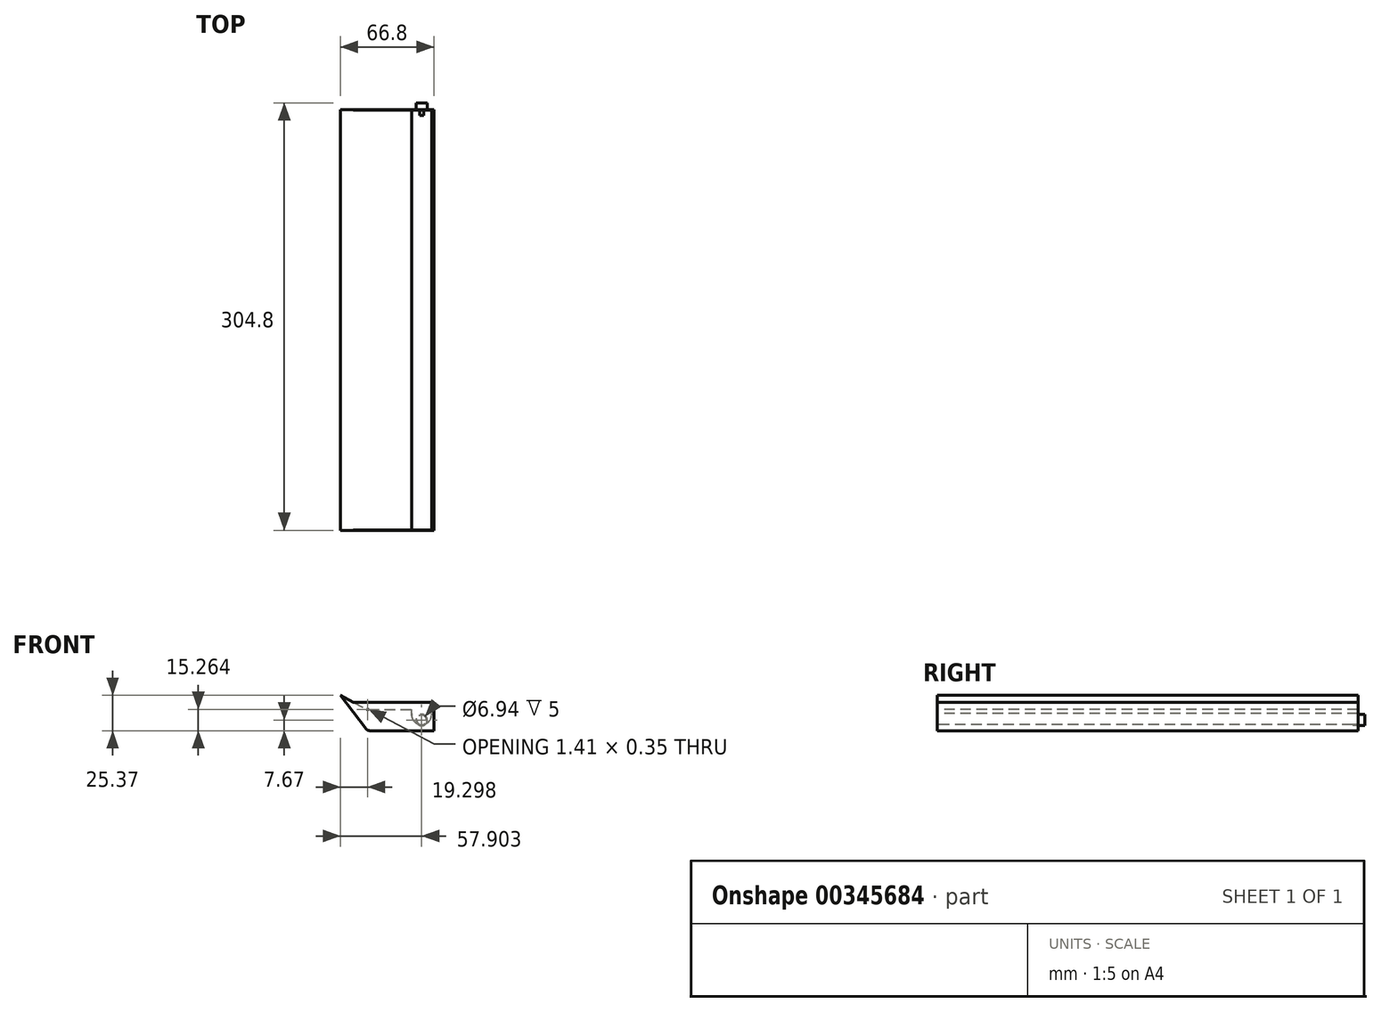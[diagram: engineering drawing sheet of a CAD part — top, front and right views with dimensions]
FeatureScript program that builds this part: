
annotation { "Feature Type Name" : "Feature", "Feature Type Description" : "" }
export const myFeature = defineFeature(function(context is Context, id is Id, definition is map)
    precondition{}
    {
        {
            var Q0;
            Q0=qCreatedBy(makeId("Front.planeOp"),FACE);
            var sketch = newSketch(context, id + "F0", { "sketchPlane" : qUnion([Q0])});
            skLineSegment(sketch, "E0", {"start": v(-53.15, 39.65) * mm, "end": v(-34.56, 29.72) * mm});
            skLineSegment(sketch, "E1", {"start": v(-33.15, 29.37) * mm, "end": v(-2.4, 29.37) * mm});
            skLineSegment(sketch, "E2", {"start": v(-2.4, 29.37) * mm, "end": v(-2.4, 26.46) * mm});
            skLineSegment(sketch, "E3", {"start": v(-2.4, 14.37) * mm, "end": v(-32.4, 14.37) * mm});
            skLineSegment(sketch, "E4", {"start": v(-34.8, 15.55) * mm, "end": v(-53.15, 39.65) * mm});
            skPoint(sketch, "E5.visualSharp", {"position": v(-33.9, 29.37) * mm});
            skArc(sketch, "E5.filletArc", {"start": v(-34.56, 29.72) * mm, "mid": v(-33.87, 29.46) * mm, "end": v(-33.15, 29.37) * mm});
            skPoint(sketch, "E6.visualSharp", {"position": v(-33.9, 14.37) * mm});
            skArc(sketch, "E6.filletArc", {"start": v(-34.8, 15.55) * mm, "mid": v(-33.74, 14.68) * mm, "end": v(-32.4, 14.37) * mm});
            skLineSegment(sketch, "E7", {"start": v(13.65, 14.28) * mm, "end": v(-2.4, 14.37) * mm});
            skLineSegment(sketch, "E8", {"start": v(13.65, 26.46) * mm, "end": v(13.65, 14.28) * mm});
            skLineSegment(sketch, "E9", {"start": v(13.65, 26.46) * mm, "end": v(13.65, 29.37) * mm});
            skLineSegment(sketch, "E10", {"start": v(13.65, 29.37) * mm, "end": v(11.79, 29.37) * mm});
            skLineSegment(sketch, "E11", {"start": v(11.79, 29.37) * mm, "end": v(11.79, 26.46) * mm});
            skArc(sketch, "E12", {"start": v(-2.4, 26.46) * mm, "mid": v(4.7, 18.65) * mm, "end": v(11.79, 26.46) * mm});
            skSolve(sketch);
        }
        {
            var Q0;
            Q0=qSketchRegion(id+"F0",true);
            extrude(context, id + "F1", {"entities" : qUnion([Q0]), "oppositeDirection" : true, "depth" : 300 * mm});
        }
        {
            var Q0;
            Q0=makeQuery(id+"F1.opExtrude","CAP_FACE",FACE,{"disambiguationData":[OSD([sQuery(id+"F0.wireOp",EDGE,"E0"),sQuery(id+"F0.wireOp",EDGE,"E1"),sQuery(id+"F0.wireOp",EDGE,"E2"),sQuery(id+"F0.wireOp",EDGE,"E3"),sQuery(id+"F0.wireOp",EDGE,"E4"),sQuery(id+"F0.wireOp",EDGE,"E5.filletArc"),sQuery(id+"F0.wireOp",EDGE,"E6.filletArc"),sQuery(id+"F0.wireOp",EDGE,"E7"),sQuery(id+"F0.wireOp",EDGE,"E8"),sQuery(id+"F0.wireOp",EDGE,"E9"),sQuery(id+"F0.wireOp",EDGE,"E10"),sQuery(id+"F0.wireOp",EDGE,"E11"),sQuery(id+"F0.wireOp",EDGE,"E12")])],"isStart":true});
            var sketch = newSketch(context, id + "F2", { "sketchPlane" : qUnion([Q0])});
            skLineSegment(sketch, "E13", {"start": v(-43.85, 34.68) * mm, "end": v(13.65, 34.68) * mm});
            skLineSegment(sketch, "E14", {"start": v(13.65, 34.68) * mm, "end": v(13.65, 29.37) * mm});
            skLineSegment(sketch, "E15", {"start": v(-43.85, 34.68) * mm, "end": v(-34.56, 29.72) * mm});
            skLineSegment(sketch, "E16", {"start": v(-34.56, 29.72) * mm, "end": v(-33.15, 29.37) * mm});
            skLineSegment(sketch, "E17", {"start": v(-33.15, 29.37) * mm, "end": v(-2.4, 29.37) * mm});
            skLineSegment(sketch, "E18", {"start": v(-2.4, 29.37) * mm, "end": v(-2.5, 18.65) * mm});
            skPoint(sketch, "E18.endSnap0", {"position": v(4.7, 18.65) * mm});
            skLineSegment(sketch, "E19", {"start": v(-2.5, 18.65) * mm, "end": v(13.65, 18.65) * mm});
            skLineSegment(sketch, "E20", {"start": v(13.65, 18.65) * mm, "end": v(13.65, 29.37) * mm});
            skSolve(sketch);
        }
        {
            var Q0;
            Q0=qSketchRegion(id+"F2",true);
            extrude(context, id + "F3", {"entities" : qUnion([Q0]), "operationType" : NewBodyOperationType.ADD, "oppositeDirection" : true, "depth" : .2 * mm});
        }
        {
            var Q0;
            Q0=makeQuery(id+"F1.opExtrude","CAP_FACE",FACE,{"disambiguationData":[OSD([sQuery(id+"F0.wireOp",EDGE,"E0"),sQuery(id+"F0.wireOp",EDGE,"E1"),sQuery(id+"F0.wireOp",EDGE,"E2"),sQuery(id+"F0.wireOp",EDGE,"E3"),sQuery(id+"F0.wireOp",EDGE,"E4"),sQuery(id+"F0.wireOp",EDGE,"E5.filletArc"),sQuery(id+"F0.wireOp",EDGE,"E6.filletArc"),sQuery(id+"F0.wireOp",EDGE,"E7"),sQuery(id+"F0.wireOp",EDGE,"E8"),sQuery(id+"F0.wireOp",EDGE,"E9"),sQuery(id+"F0.wireOp",EDGE,"E10"),sQuery(id+"F0.wireOp",EDGE,"E11"),sQuery(id+"F0.wireOp",EDGE,"E12")])],"isStart":false});
            var sketch = newSketch(context, id + "F4", { "sketchPlane" : qUnion([Q0])});
            skLineSegment(sketch, "E21", {"start": v(43.85, 34.68) * mm, "end": v(-13.65, 34.68) * mm});
            skLineSegment(sketch, "E22", {"start": v(-13.65, 34.68) * mm, "end": v(-13.65, 18.65) * mm});
            skPoint(sketch, "E22.endSnap0", {"position": v(-4.7, 18.65) * mm});
            skLineSegment(sketch, "E23", {"start": v(-13.65, 18.65) * mm, "end": v(2.4, 18.65) * mm});
            skLineSegment(sketch, "E24", {"start": v(2.4, 18.65) * mm, "end": v(2.4, 29.37) * mm});
            skLineSegment(sketch, "E25", {"start": v(2.4, 29.37) * mm, "end": v(33.15, 29.37) * mm});
            skLineSegment(sketch, "E26", {"start": v(33.15, 29.37) * mm, "end": v(34.56, 29.72) * mm});
            skLineSegment(sketch, "E27", {"start": v(34.56, 29.72) * mm, "end": v(43.85, 34.68) * mm});
            skSolve(sketch);
        }
        {
            var Q0;
            Q0=qSketchRegion(id+"F4",true);
            extrude(context, id + "F5", {"entities" : qUnion([Q0]), "operationType" : NewBodyOperationType.ADD, "oppositeDirection" : true, "depth" : .2 * mm});
        }
        {
            var Q0;
            Q0=makeQuery(id+"F5.boolean.opBoolean","MERGE",FACE,{"derivedFrom":[makeQuery(id+"F3.boolean.opBoolean","MERGE",FACE,{"derivedFrom":[makeQuery(id+"F1.opExtrude","SWEPT_FACE",FACE,{"disambiguationData":[OSD([sQuery(id+"F0.wireOp",EDGE,"E8"),sQuery(id+"F0.wireOp",EDGE,"E9")])]}),makeQuery(id+"F3.opExtrude","SWEPT_FACE",FACE,{"disambiguationData":[OSD([sQuery(id+"F2.wireOp",EDGE,"E14"),sQuery(id+"F2.wireOp",EDGE,"E20")])]})]}),makeQuery(id+"F5.opExtrude","SWEPT_FACE",FACE,{"disambiguationData":[OSD([sQuery(id+"F4.wireOp",EDGE,"E22")])]})]});
            var sketch = newSketch(context, id + "F6", { "sketchPlane" : qUnion([Q0])});
            skLineSegment(sketch, "E28", {"start": v(0.2, 34.68) * mm, "end": v(300, 34.68) * mm});
            skLineSegment(sketch, "E29", {"start": v(300, 34.68) * mm, "end": v(299.8, 29.37) * mm});
            skLineSegment(sketch, "E30", {"start": v(299.8, 29.37) * mm, "end": v(0.2, 29.37) * mm});
            skLineSegment(sketch, "E31", {"start": v(0.2, 29.37) * mm, "end": v(0.2, 34.68) * mm});
            skSolve(sketch);
        }
        {
            var Q0;
            Q0=qSketchRegion(id+"F6",true);
            extrude(context, id + "F7", {"entities" : qUnion([Q0]), "oppositeDirection" : true, "depth" : 1.8 * mm});
        }
        {
            var Q0;
            Q0=makeQuery(id+"F5.opExtrude","CAP_FACE",FACE,{"disambiguationData":[OSD([sQuery(id+"F4.wireOp",EDGE,"E21"),sQuery(id+"F4.wireOp",EDGE,"E22"),sQuery(id+"F4.wireOp",EDGE,"E23"),sQuery(id+"F4.wireOp",EDGE,"E24"),sQuery(id+"F4.wireOp",EDGE,"E25"),sQuery(id+"F4.wireOp",EDGE,"E26"),sQuery(id+"F4.wireOp",EDGE,"E27")])],"isStart":false});
            var sketch = newSketch(context, id + "F8", { "sketchPlane" : qUnion([Q0])});
            skCircle(sketch, "E32", {"center": v(4.75, 21.95) * mm, "radius": 3.47 * mm});
            skCircle(sketch, "E33", {"center": v(4.75, 21.95) * mm, "radius": 4.03 * mm});
            skCircle(sketch, "E34", {"center": v(4.75, 21.95) * mm, "radius": 3.4 * mm});
            skSolve(sketch);
        }
        {
            var Q0;
            Q0=qSketchRegion(id+"F8",true);
            extrude(context, id + "F9", {"entities" : qUnion([Q0]), "operationType" : NewBodyOperationType.REMOVE, "depth" : 0.01 * mm});
        }
        {
            var Q0;
            Q0=qSketchRegion(id+"F8",true);
            extrude(context, id + "F10", {"entities" : qUnion([Q0]), "operationType" : NewBodyOperationType.ADD, "oppositeDirection" : true, "depth" : 5 * mm});
        }
        {
            var Q0;
            Q0=makeQuery(id+"F10.boolean.opBoolean","SPLIT",FACE,{"disambiguationData":[TD([makeQuery(id+"F10.opExtrude","SWEPT_FACE",FACE,{"disambiguationData":[OSD([sQuery(id+"F8.wireOp",EDGE,"E32")])]})])],"derivedFrom":makeQuery(id+"F5.boolean.opBoolean","MERGE",FACE,{"derivedFrom":[makeQuery(id+"F1.opExtrude","CAP_FACE",FACE,{"disambiguationData":[OSD([sQuery(id+"F0.wireOp",EDGE,"E0"),sQuery(id+"F0.wireOp",EDGE,"E1"),sQuery(id+"F0.wireOp",EDGE,"E2"),sQuery(id+"F0.wireOp",EDGE,"E3"),sQuery(id+"F0.wireOp",EDGE,"E4"),sQuery(id+"F0.wireOp",EDGE,"E5.filletArc"),sQuery(id+"F0.wireOp",EDGE,"E6.filletArc"),sQuery(id+"F0.wireOp",EDGE,"E7"),sQuery(id+"F0.wireOp",EDGE,"E8"),sQuery(id+"F0.wireOp",EDGE,"E9"),sQuery(id+"F0.wireOp",EDGE,"E10"),sQuery(id+"F0.wireOp",EDGE,"E11"),sQuery(id+"F0.wireOp",EDGE,"E12")])],"isStart":false}),makeQuery(id+"F5.opExtrude","CAP_FACE",FACE,{"disambiguationData":[OSD([sQuery(id+"F4.wireOp",EDGE,"E21"),sQuery(id+"F4.wireOp",EDGE,"E22"),sQuery(id+"F4.wireOp",EDGE,"E23"),sQuery(id+"F4.wireOp",EDGE,"E24"),sQuery(id+"F4.wireOp",EDGE,"E25"),sQuery(id+"F4.wireOp",EDGE,"E26"),sQuery(id+"F4.wireOp",EDGE,"E27")])],"isStart":true})]})});
            extrude(context, id + "F11", {"entities" : qUnion([Q0]), "operationType" : NewBodyOperationType.REMOVE, "oppositeDirection" : true, "depth" : 4 * mm});
        }
        {
            var Q0;
            Q0=makeQuery(id+"F7.opExtrude","SWEPT_BODY",BODY,{"disambiguationData":[OSD([sQuery(id+"F6.wireOp",EDGE,"E28"),sQuery(id+"F6.wireOp",EDGE,"E29"),sQuery(id+"F6.wireOp",EDGE,"E30"),sQuery(id+"F6.wireOp",EDGE,"E31")])]});
            deleteBodies(context, id + "F12", {"entities" : qUnion([Q0])});
        }
        {
            var Q0;
            Q0=makeQuery(id+"F1.opExtrude","SWEPT_FACE",FACE,{"disambiguationData":[OSD([sQuery(id+"F0.wireOp",EDGE,"E10")])]});
            extrude(context, id + "F13", {"entities" : qUnion([Q0]), "operationType" : NewBodyOperationType.ADD, "depth" : 5.32 * mm});
        }
    });
